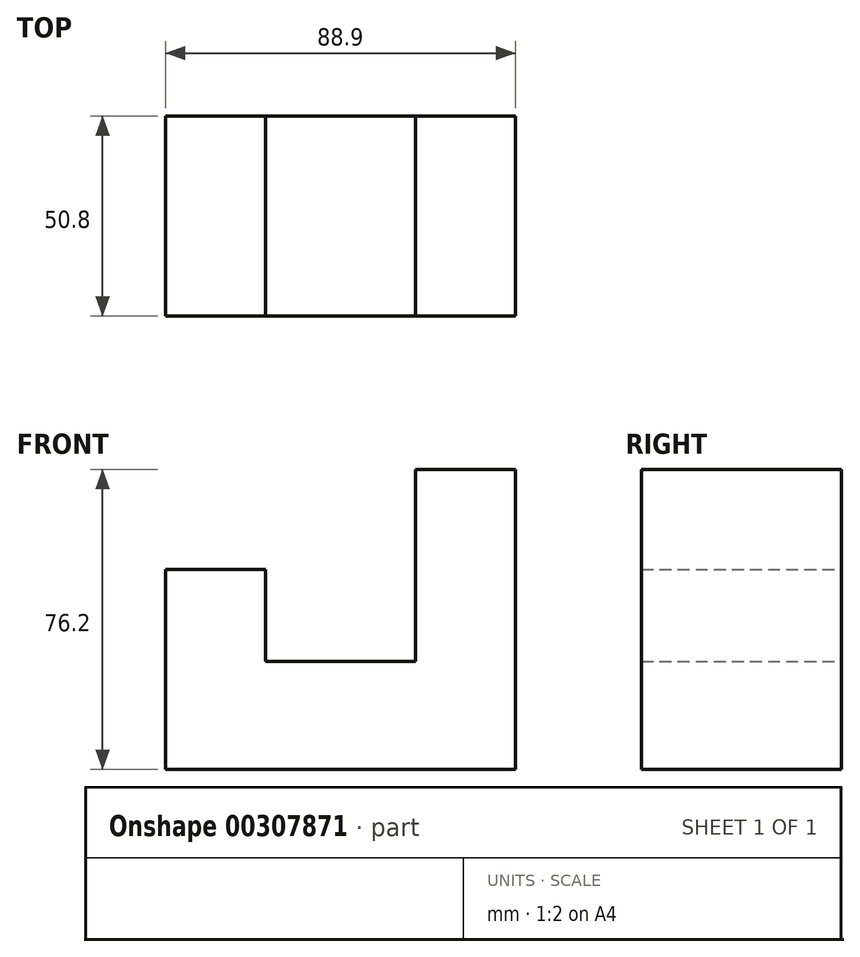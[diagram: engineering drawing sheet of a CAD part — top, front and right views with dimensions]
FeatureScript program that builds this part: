
annotation { "Feature Type Name" : "Feature", "Feature Type Description" : "" }
export const myFeature = defineFeature(function(context is Context, id is Id, definition is map)
    precondition{}
    {
        {
            var Q0;
            Q0=qCreatedBy(makeId("Front.planeOp"),FACE);
            var sketch = newSketch(context, id + "F0", { "sketchPlane" : qUnion([Q0])});
            skLineSegment(sketch, "E0", {"start": v(-43.83, -36.96) * mm, "end": v(45.07, -36.96) * mm});
            skLineSegment(sketch, "E1", {"start": v(45.07, -36.96) * mm, "end": v(45.07, 39.24) * mm});
            skLineSegment(sketch, "E2", {"start": v(45.07, 39.24) * mm, "end": v(19.67, 39.24) * mm});
            skLineSegment(sketch, "E3", {"start": v(19.67, 39.24) * mm, "end": v(19.67, -9.52) * mm});
            skLineSegment(sketch, "E4", {"start": v(19.67, -9.52) * mm, "end": v(-18.43, -9.52) * mm});
            skLineSegment(sketch, "E5", {"start": v(-18.43, -9.52) * mm, "end": v(-18.43, 13.84) * mm});
            skLineSegment(sketch, "E6", {"start": v(-18.43, 13.84) * mm, "end": v(-43.83, 13.84) * mm});
            skLineSegment(sketch, "E7", {"start": v(-43.83, 13.84) * mm, "end": v(-43.83, -36.96) * mm});
            skSolve(sketch);
        }
        {
            var Q0;
            Q0=makeQuery(id+"F0.imprint","IMPRINT",FACE,{"disambiguationData":[TD([[makeQuery(id+"F0.imprint","IMPRINT",EDGE,{"derivedFrom":sQuery(id+"F0.wireOp",EDGE,"E0")}),1.0]])]});
            extrude(context, id + "F1", {"entities" : qUnion([Q0]), "depth" : 50.8 * mm});
        }
    });
